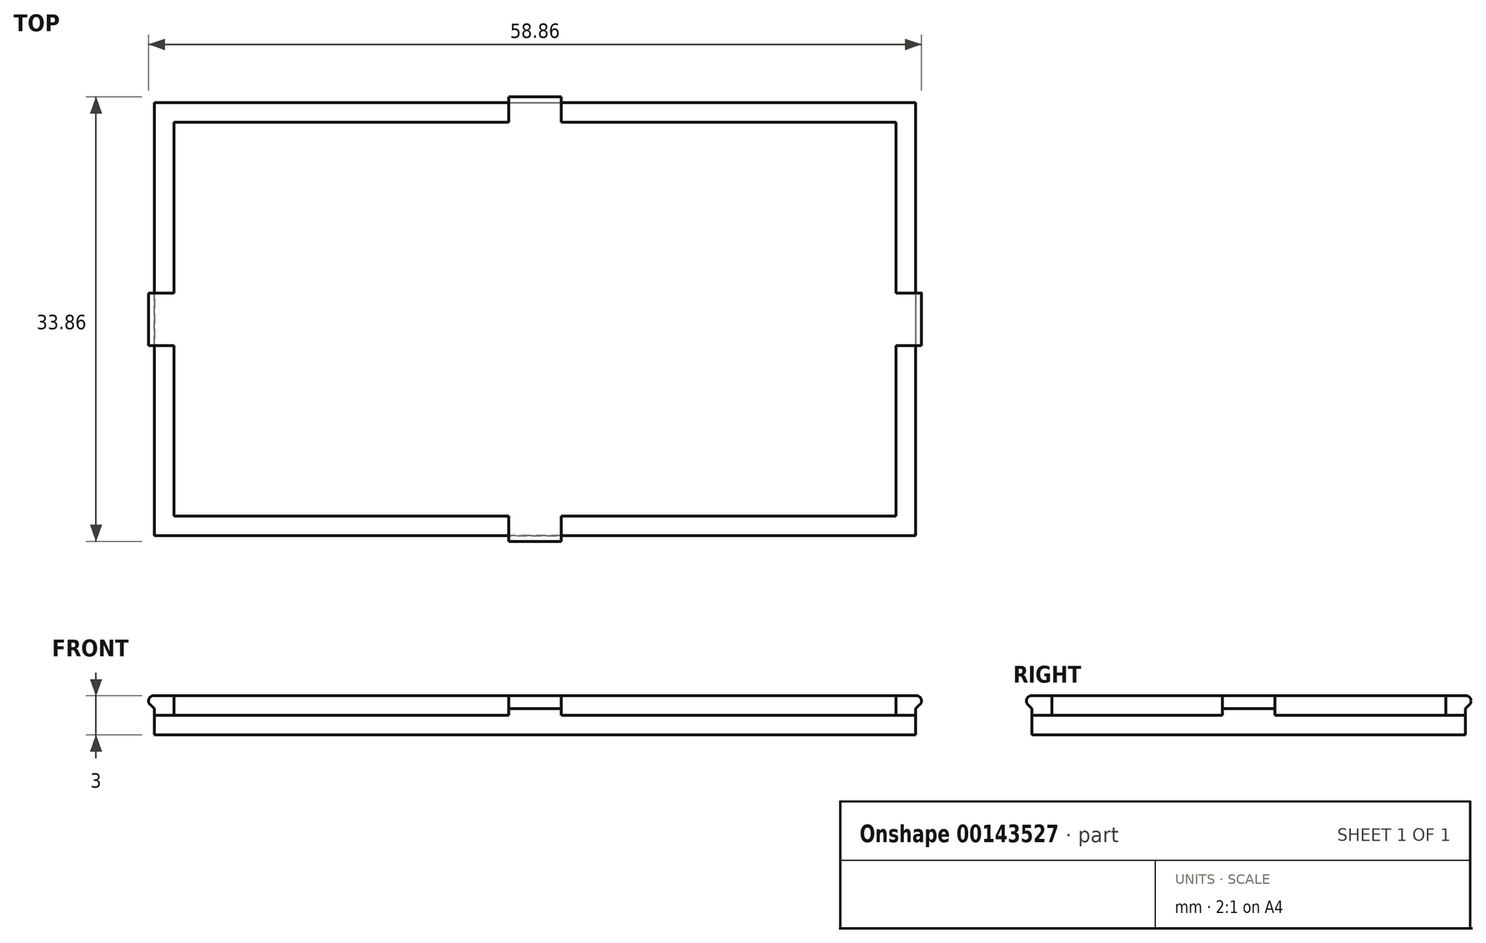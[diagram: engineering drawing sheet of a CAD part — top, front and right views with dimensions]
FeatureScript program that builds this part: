
annotation { "Feature Type Name" : "Feature", "Feature Type Description" : "" }
export const myFeature = defineFeature(function(context is Context, id is Id, definition is map)
    precondition{}
    {
        {
            var Q0;
            Q0=qCreatedBy(makeId("Top.planeOp"),FACE);
            var sketch = newSketch(context, id + "F0", { "sketchPlane" : qUnion([Q0])});
            skLineSegment(sketch, "E0.bottom", {"start": v(-29, 16.5) * mm, "end": v(29, 16.5) * mm});
            skLineSegment(sketch, "E0.top", {"start": v(-29, -16.5) * mm, "end": v(29, -16.5) * mm});
            skLineSegment(sketch, "E0.left", {"start": v(-29, 16.5) * mm, "end": v(-29, -16.5) * mm});
            skLineSegment(sketch, "E0.right", {"start": v(29, 16.5) * mm, "end": v(29, -16.5) * mm});
            skSolve(sketch);
        }
        {
            var Q0;
            Q0 = qSketchRegion(id + "F0", true);
            extrude(context, id + "F1", {"entities" : qUnion([Q0]), "depth" : 1.5 * mm});
        }
        {
            var Q0;
            Q0=makeQuery(id+"F1.opExtrude","CAP_FACE",FACE,{"disambiguationData":[OSD([sQuery(id+"F0.wireOp",EDGE,"E0.bottom"),sQuery(id+"F0.wireOp",EDGE,"E0.top"),sQuery(id+"F0.wireOp",EDGE,"E0.left"),sQuery(id+"F0.wireOp",EDGE,"E0.right")])],"isStart":false});
            var sketch = newSketch(context, id + "F2", { "sketchPlane" : qUnion([Q0])});
            skLineSegment(sketch, "E1.bottom", {"start": v(-27.5, 15) * mm, "end": v(27.5, 15) * mm});
            skLineSegment(sketch, "E1.top", {"start": v(-27.5, -15) * mm, "end": v(27.5, -15) * mm});
            skLineSegment(sketch, "E1.left", {"start": v(-27.5, 15) * mm, "end": v(-27.5, -15) * mm});
            skLineSegment(sketch, "E1.right", {"start": v(27.5, 15) * mm, "end": v(27.5, -15) * mm});
            skSolve(sketch);
        }
        {
            var Q0;
            Q0 = qSketchRegion(id + "F2", true);
            extrude(context, id + "F3", {"entities" : qUnion([Q0]), "operationType" : NewBodyOperationType.ADD, "depth" : 1.5 * mm});
        }
        {
            var Q0;
            Q0=makeQuery(id+"F1.opExtrude","CAP_FACE",FACE,{"disambiguationData":[OSD([sQuery(id+"F0.wireOp",EDGE,"E0.bottom"),sQuery(id+"F0.wireOp",EDGE,"E0.top"),sQuery(id+"F0.wireOp",EDGE,"E0.left"),sQuery(id+"F0.wireOp",EDGE,"E0.right")])],"isStart":false});
            var sketch = newSketch(context, id + "F4", { "sketchPlane" : qUnion([Q0])});
            skLineSegment(sketch, "E2.bottom", {"start": v(-29, 2) * mm, "end": v(-27.5, 2) * mm});
            skLineSegment(sketch, "E2.top", {"start": v(-29, -2) * mm, "end": v(-27.5, -2) * mm});
            skLineSegment(sketch, "E2.left", {"start": v(-29, 2) * mm, "end": v(-29, -2) * mm});
            skLineSegment(sketch, "E2.right", {"start": v(-27.5, 2) * mm, "end": v(-27.5, -2) * mm});
            skLineSegment(sketch, "E3.bottom", {"start": v(-2, 16.5) * mm, "end": v(2, 16.5) * mm});
            skLineSegment(sketch, "E3.top", {"start": v(-2, 15) * mm, "end": v(2, 15) * mm});
            skLineSegment(sketch, "E3.left", {"start": v(-2, 16.5) * mm, "end": v(-2, 15) * mm});
            skLineSegment(sketch, "E3.right", {"start": v(2, 16.5) * mm, "end": v(2, 15) * mm});
            skLineSegment(sketch, "E4.bottom", {"start": v(29, 2) * mm, "end": v(27.5, 2) * mm});
            skLineSegment(sketch, "E4.top", {"start": v(29, -2) * mm, "end": v(27.5, -2) * mm});
            skLineSegment(sketch, "E4.left", {"start": v(29, 2) * mm, "end": v(29, -2) * mm});
            skLineSegment(sketch, "E4.right", {"start": v(27.5, 2) * mm, "end": v(27.5, -2) * mm});
            skLineSegment(sketch, "E5.bottom", {"start": v(2, -16.5) * mm, "end": v(-2, -16.5) * mm});
            skLineSegment(sketch, "E5.top", {"start": v(2, -15) * mm, "end": v(-2, -15) * mm});
            skLineSegment(sketch, "E5.left", {"start": v(2, -16.5) * mm, "end": v(2, -15) * mm});
            skLineSegment(sketch, "E5.right", {"start": v(-2, -16.5) * mm, "end": v(-2, -15) * mm});
            skSolve(sketch);
        }
        {
            var Q0;
            Q0 = qSketchRegion(id + "F4", true);
            extrude(context, id + "F5", {"entities" : qUnion([Q0]), "operationType" : NewBodyOperationType.ADD, "depth" : 1.5 * mm});
        }
        {
            var Q0;
            Q0=makeQuery(id+"F5.opExtrude","SWEPT_FACE",FACE,{"disambiguationData":[OSD([sQuery(id+"F4.wireOp",EDGE,"E5.right")])]});
            var sketch = newSketch(context, id + "F6", { "sketchPlane" : qUnion([Q0])});
            skLineSegment(sketch, "E6", {"start": v(16.5, 3) * mm, "end": v(17.5, 3) * mm});
            skLineSegment(sketch, "E7", {"start": v(17.5, 3) * mm, "end": v(16.5, 2) * mm});
            skLineSegment(sketch, "E8", {"start": v(16.5, 3) * mm, "end": v(16.5, 2) * mm});
            skSolve(sketch);
        }
        {
            var Q0;
            Q0 = qSketchRegion(id + "F6", true);
            extrude(context, id + "F7", {"entities" : qUnion([Q0]), "operationType" : NewBodyOperationType.ADD, "oppositeDirection" : true, "depth" : 4 * mm});
        }
        {
            var Q0;
            Q0=makeQuery(id+"F5.opExtrude","SWEPT_FACE",FACE,{"disambiguationData":[OSD([sQuery(id+"F4.wireOp",EDGE,"E4.top")])]});
            var sketch = newSketch(context, id + "F8", { "sketchPlane" : qUnion([Q0])});
            skLineSegment(sketch, "E9", {"start": v(29, 3) * mm, "end": v(30, 3) * mm});
            skLineSegment(sketch, "E10", {"start": v(30, 3) * mm, "end": v(29, 2) * mm});
            skLineSegment(sketch, "E11", {"start": v(29, 2) * mm, "end": v(29, 3) * mm});
            skSolve(sketch);
        }
        {
            var Q0;
            Q0 = qSketchRegion(id + "F8", true);
            extrude(context, id + "F9", {"entities" : qUnion([Q0]), "operationType" : NewBodyOperationType.ADD, "oppositeDirection" : true, "depth" : 4 * mm});
        }
        {
            var Q0;
            Q0=makeQuery(id+"F5.opExtrude","SWEPT_FACE",FACE,{"disambiguationData":[OSD([sQuery(id+"F4.wireOp",EDGE,"E2.bottom")])]});
            var sketch = newSketch(context, id + "F10", { "sketchPlane" : qUnion([Q0])});
            skLineSegment(sketch, "E12", {"start": v(29, 3) * mm, "end": v(30, 3) * mm});
            skLineSegment(sketch, "E13", {"start": v(30, 3) * mm, "end": v(29, 2) * mm});
            skLineSegment(sketch, "E14", {"start": v(29, 2) * mm, "end": v(29, 3) * mm});
            skSolve(sketch);
        }
        {
            var Q0;
            Q0 = qSketchRegion(id + "F10", true);
            extrude(context, id + "F11", {"entities" : qUnion([Q0]), "operationType" : NewBodyOperationType.ADD, "oppositeDirection" : true, "depth" : 4 * mm});
        }
        {
            var Q0;
            Q0=makeQuery(id+"F5.opExtrude","SWEPT_FACE",FACE,{"disambiguationData":[OSD([sQuery(id+"F4.wireOp",EDGE,"E3.right")])]});
            var sketch = newSketch(context, id + "F12", { "sketchPlane" : qUnion([Q0])});
            skLineSegment(sketch, "E15", {"start": v(16.5, 3) * mm, "end": v(17.5, 3) * mm});
            skLineSegment(sketch, "E16", {"start": v(17.5, 3) * mm, "end": v(16.5, 2) * mm});
            skLineSegment(sketch, "E17", {"start": v(16.5, 2) * mm, "end": v(16.5, 3) * mm});
            skSolve(sketch);
        }
        {
            var Q0;
            Q0 = qSketchRegion(id + "F12", true);
            extrude(context, id + "F13", {"entities" : qUnion([Q0]), "operationType" : NewBodyOperationType.ADD, "oppositeDirection" : true, "depth" : 4 * mm});
        }
        {
            var Q0;
            Q0=makeQuery(id+"F9.opExtrude","SWEPT_EDGE",EDGE,{"disambiguationData":[OSD([sQuery(id+"F8.wireOp",EDGE,"E9"),sQuery(id+"F8.wireOp",EDGE,"E10")])]});
            var Q1;
            Q1=makeQuery(id+"F13.opExtrude","SWEPT_EDGE",EDGE,{"disambiguationData":[OSD([sQuery(id+"F12.wireOp",EDGE,"E15"),sQuery(id+"F12.wireOp",EDGE,"E16")])]});
            var Q2;
            Q2=makeQuery(id+"F11.opExtrude","SWEPT_EDGE",EDGE,{"disambiguationData":[OSD([sQuery(id+"F10.wireOp",EDGE,"E12"),sQuery(id+"F10.wireOp",EDGE,"E13")])]});
            var Q3;
            Q3=makeQuery(id+"F7.opExtrude","SWEPT_EDGE",EDGE,{"disambiguationData":[OSD([sQuery(id+"F6.wireOp",EDGE,"E6"),sQuery(id+"F6.wireOp",EDGE,"E7")])]});
            fillet(context, id + "F14", {"entities" : qUnion([Q0, Q1, Q2, Q3]), "radius" : .4 * mm, "tangentPropagation" : true, "allowEdgeOverflow" : false});
        }
    });
